# Revit family: Magnuson-Croma-Planters+
name_source: partatom
category: Furniture
units: mm (PartAtom-declared; Revit-internal decimal feet)

## family parameters
Always vertical = Yes
Cut with Voids When Loaded = No
OmniClass Number = 23.40.20.00
OmniClass Title = General Furniture and Specialties
Room Calculation Point = No
Shared = No
Work Plane-Based = No

## types (3) — shared parameters
Case Finish = MAG - Aluminum Paint Sand
Default Elevation = 0"
Description = Planter Made of aluminum and available in three different sizes, with capacities of 15, 36, and 40 liters.
Glide Finish = MAG - Plastic Black
Keynote = 12500
Leg Finish = MAG - Aluminum Paint Sand
Low Emitting Finish = Yes
Low Emitting Material = Yes
Manufacturer = Magnuson Group
Plant Pot = MAG - Plastic Black
Product Documentation Link = https://st-systemtronic.com
Revit File Built By = https://servex-us.com
Salvage or Reuse = Yes
Type Comments = Croma Planter
URL = https://www.magnusongroup.com
zero-valued in all types: Percentage of Recycled Content

## per-type parameters (varying)
| type | Assembly Code | Diameter | Height | Height Case | Height Leg | Leg Spread |
| PLANTER L | E2020200 | 20 25/64" | 22 15/64" | 16 11/32" | 7 7/8" | 7" |
| PLANTER M |  | 17 7/16" | 27 11/64" | 15 5/32" | 14" | 5 1/2" |
| PLANTER S | E20202000 | 15 5/64" | 19 11/16" | 13 3/4" | 7 7/8" | 4 5/16" |

note: column(s) folded — value = type name in every type: Model

## geometry (parser evidence)
native form markers: Sweep x5
no freeform markers — native parametric forms only
